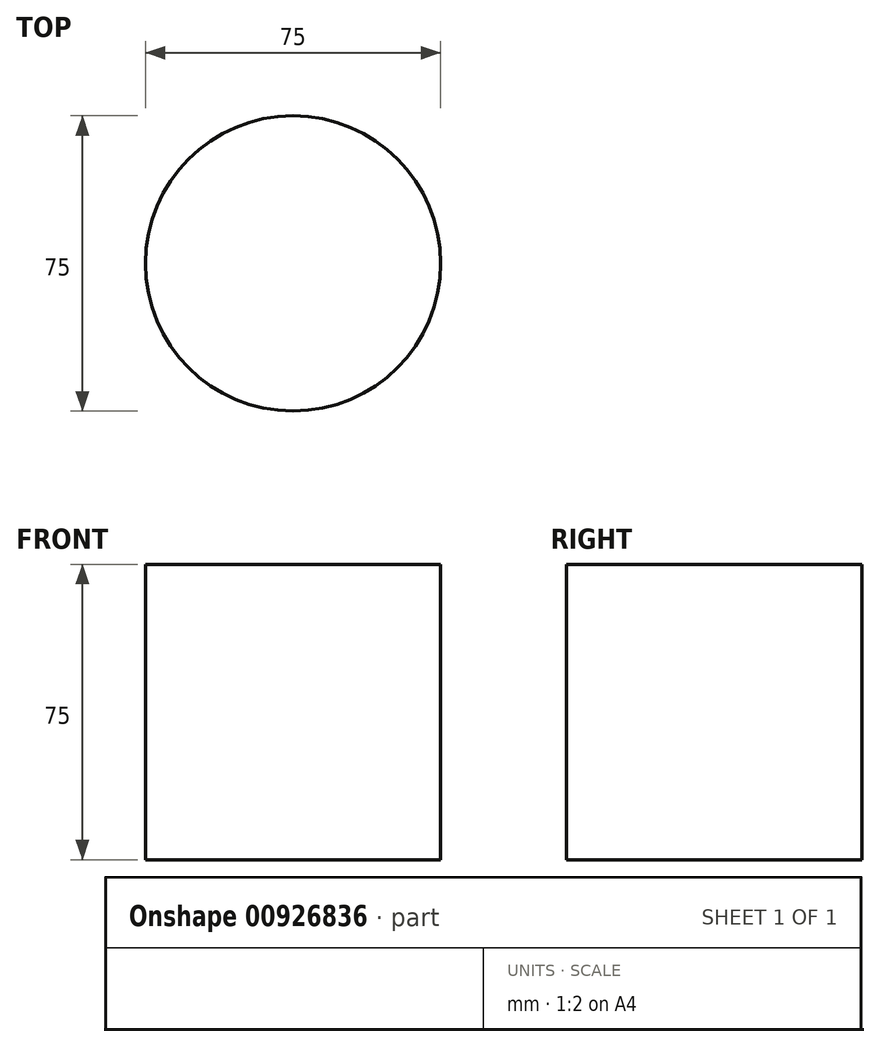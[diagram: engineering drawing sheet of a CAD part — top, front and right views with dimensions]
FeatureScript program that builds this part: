
annotation { "Feature Type Name" : "Feature", "Feature Type Description" : "" }
export const myFeature = defineFeature(function(context is Context, id is Id, definition is map)
    precondition{}
    {
        {
            var Q0;
            Q0=qCreatedBy(makeId("Top.planeOp"),FACE);
            var sketch = newSketch(context, id + "F0", { "sketchPlane" : qUnion([Q0])});
            skCircle(sketch, "E0", {"center": v(0, 0) * mm, "radius": 37.5 * mm});
            skSolve(sketch);
        }
        {
            var Q0;
            Q0=makeQuery(id+"F0.imprint","IMPRINT",FACE,{"disambiguationData":[TD([[makeQuery(id+"F0.imprint","IMPRINT",EDGE,{"derivedFrom":sQuery(id+"F0.wireOp",EDGE,"E0")}),1.0]])]});
            var Q1;
            Q1 = qSketchRegion(id + "F0", true);
            extrude(context, id + "F1", {"entities" : qUnion([Q0, Q1]), "depth" : 75 * mm, "offsetDistance" : 25 * mm});
        }
    });
